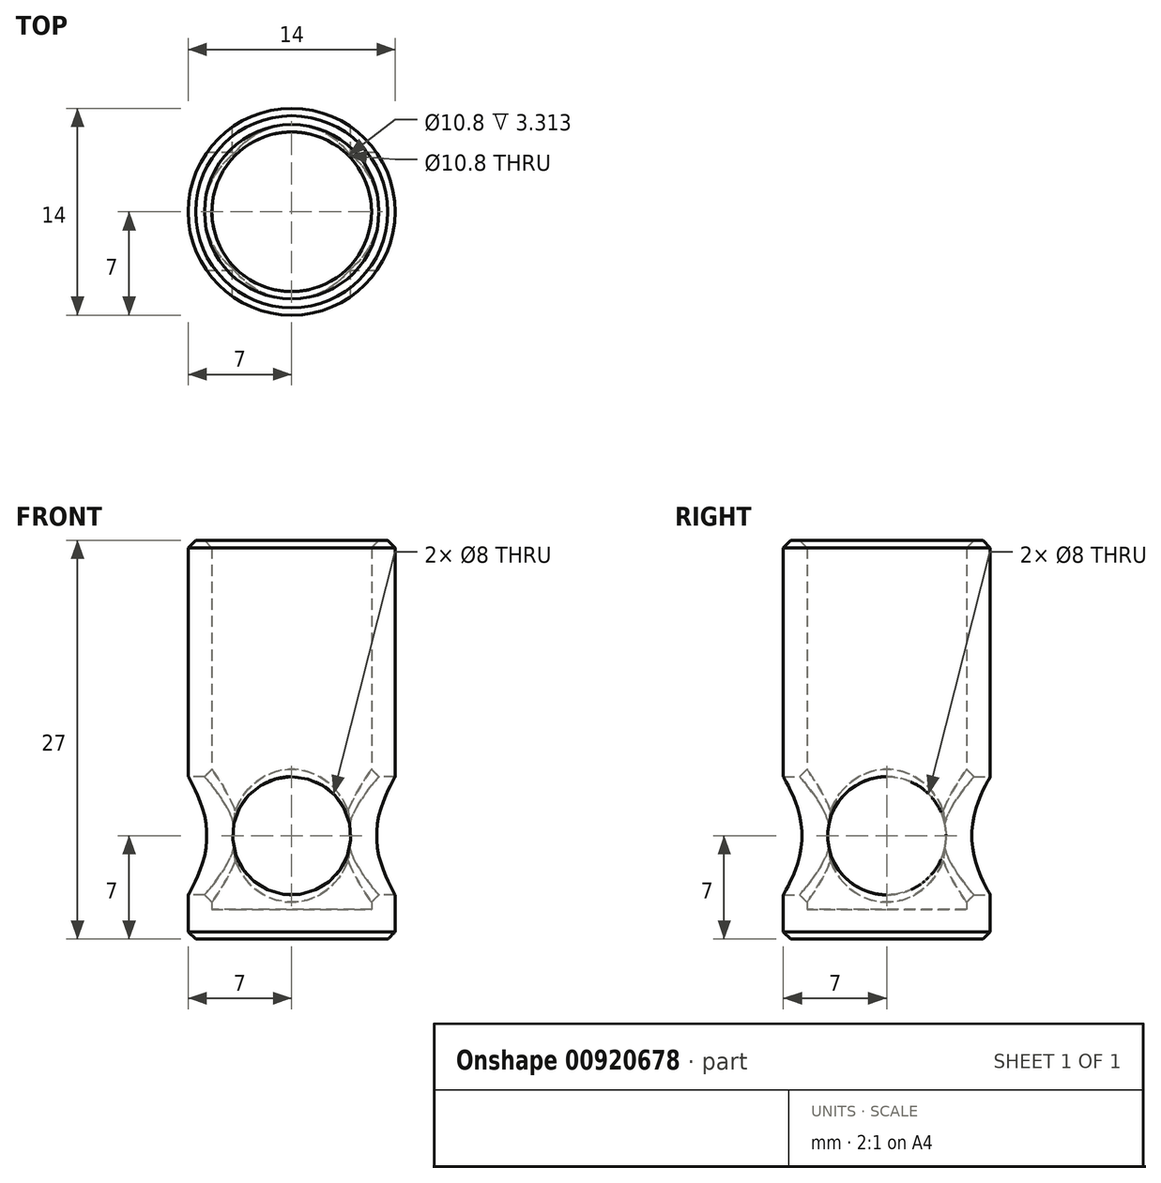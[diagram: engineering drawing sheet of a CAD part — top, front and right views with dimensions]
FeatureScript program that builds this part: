
annotation { "Feature Type Name" : "Feature", "Feature Type Description" : "" }
export const myFeature = defineFeature(function(context is Context, id is Id, definition is map)
    precondition{}
    {
        {
            var Q0;
            Q0=qCreatedBy(makeId("Top.planeOp"),FACE);
            var sketch = newSketch(context, id + "F0", { "sketchPlane" : qUnion([Q0])});
            skCircle(sketch, "E0", {"center": v(0, 0) * mm, "radius": 5.4 * mm});
            skCircle(sketch, "E1", {"center": v(0, 0) * mm, "radius": 7 * mm});
            skSolve(sketch);
        }
        {
            var Q0;
            Q0=makeQuery(id+"F0.imprint","IMPRINT",FACE,{"disambiguationData":[TD([[makeQuery(id+"F0.imprint","IMPRINT",EDGE,{"derivedFrom":sQuery(id+"F0.wireOp",EDGE,"E0")}),-1.0]])]});
            extrude(context, id + "F1", {"entities" : qUnion([Q0]), "depth" : 25 * mm, "offsetDistance" : 25 * mm});
        }
        {
            var Q0;
            Q0=makeQuery(id+"F1.opExtrude","CAP_FACE",FACE,{"disambiguationData":[OSD([sQuery(id+"F0.wireOp",EDGE,"E0"),sQuery(id+"F0.wireOp",EDGE,"E1")])],"isStart":true});
            var Q1;
            Q1=makeQuery(id+"F0.imprint","IMPRINT",FACE,{"disambiguationData":[TD([[makeQuery(id+"F0.imprint","IMPRINT",EDGE,{"derivedFrom":sQuery(id+"F0.wireOp",EDGE,"E0")}),1.0]])]});
            extrude(context, id + "F2", {"entities" : qUnion([Q0, Q1]), "operationType" : NewBodyOperationType.ADD, "depth" : 2 * mm, "offsetDistance" : 25 * mm});
        }
        {
            var Q0;
            Q0=qCreatedBy(makeId("Front.planeOp"),FACE);
            var sketch = newSketch(context, id + "F3", { "sketchPlane" : qUnion([Q0])});
            skPoint(sketch, "E2", {"position": v(0, 0) * mm});
            skPoint(sketch, "E3", {"position": v(0, 5) * mm});
            skCircle(sketch, "E4", {"center": v(0, 5) * mm, "radius": 4 * mm});
            skSolve(sketch);
        }
        {
            var Q0;
            Q0=makeQuery(id+"F3.imprint","IMPRINT",FACE,{"disambiguationData":[TD([[makeQuery(id+"F3.imprint","IMPRINT",EDGE,{"derivedFrom":sQuery(id+"F3.wireOp",EDGE,"E4")}),1.0]])]});
            extrude(context, id + "F4", {"entities" : qUnion([Q0]), "operationType" : NewBodyOperationType.REMOVE, "endBound" : BoundingType.SYMMETRIC, "depth" : 25 * mm, "offsetDistance" : 25 * mm});
        }
        {
            var Q0;
            Q0=qCreatedBy(makeId("Right.planeOp"),FACE);
            var sketch = newSketch(context, id + "F5", { "sketchPlane" : qUnion([Q0])});
            skPoint(sketch, "E5", {"position": v(0, -3.33) * mm});
            skPoint(sketch, "E6", {"position": v(0, 5) * mm});
            skCircle(sketch, "E7", {"center": v(0, 5) * mm, "radius": 4 * mm});
            skSolve(sketch);
        }
        {
            var Q0;
            Q0=makeQuery(id+"F5.imprint","IMPRINT",FACE,{"disambiguationData":[TD([[makeQuery(id+"F5.imprint","IMPRINT",EDGE,{"derivedFrom":sQuery(id+"F5.wireOp",EDGE,"E7")}),1.0]])]});
            extrude(context, id + "F6", {"entities" : qUnion([Q0]), "operationType" : NewBodyOperationType.REMOVE, "endBound" : BoundingType.SYMMETRIC, "depth" : 25 * mm, "offsetDistance" : 25 * mm});
        }
        {
            var Q0;
            Q0=makeQuery(id+"F1.opExtrude","CAP_EDGE",EDGE,{"disambiguationData":[OSD([sQuery(id+"F0.wireOp",EDGE,"E0")])],"isStart":false});
            var Q1;
            Q1=makeQuery(id+"F1.opExtrude","CAP_EDGE",EDGE,{"disambiguationData":[OSD([sQuery(id+"F0.wireOp",EDGE,"E1")])],"isStart":false});
            var Q2;
            Q2=makeQuery(id+"F6.boolean.opBoolean","SPLIT",EDGE,{"disambiguationData":[OD(1.0)],"derivedFrom":makeQuery(id+"F4.boolean.opBoolean","INTERSECT",EDGE,{"disambiguationData":[OD(0.0)],"derivedFrom":[makeQuery(id+"F1.opExtrude","SWEPT_FACE",FACE,{"disambiguationData":[OSD([sQuery(id+"F0.wireOp",EDGE,"E0")])]}),makeQuery(id+"F4.opExtrude","SWEPT_FACE",FACE,{"disambiguationData":[OSD([sQuery(id+"F3.wireOp",EDGE,"E4")])]})]})});
            var Q3;
            Q3=makeQuery(id+"F6.boolean.opBoolean","INTERSECT",EDGE,{"disambiguationData":[OD(3.0)],"derivedFrom":[makeQuery(id+"F1.opExtrude","SWEPT_FACE",FACE,{"disambiguationData":[OSD([sQuery(id+"F0.wireOp",EDGE,"E0")])]}),makeQuery(id+"F6.opExtrude","SWEPT_FACE",FACE,{"disambiguationData":[OSD([sQuery(id+"F5.wireOp",EDGE,"E7")])]})]});
            var Q4;
            Q4=makeQuery(id+"F6.boolean.opBoolean","SPLIT",EDGE,{"disambiguationData":[OD(1.0)],"derivedFrom":makeQuery(id+"F4.boolean.opBoolean","INTERSECT",EDGE,{"disambiguationData":[OD(1.0)],"derivedFrom":[makeQuery(id+"F1.opExtrude","SWEPT_FACE",FACE,{"disambiguationData":[OSD([sQuery(id+"F0.wireOp",EDGE,"E0")])]}),makeQuery(id+"F4.opExtrude","SWEPT_FACE",FACE,{"disambiguationData":[OSD([sQuery(id+"F3.wireOp",EDGE,"E4")])]})]})});
            var Q5;
            Q5=makeQuery(id+"F6.boolean.opBoolean","INTERSECT",EDGE,{"disambiguationData":[OD(2.0)],"derivedFrom":[makeQuery(id+"F1.opExtrude","SWEPT_FACE",FACE,{"disambiguationData":[OSD([sQuery(id+"F0.wireOp",EDGE,"E0")])]}),makeQuery(id+"F6.opExtrude","SWEPT_FACE",FACE,{"disambiguationData":[OSD([sQuery(id+"F5.wireOp",EDGE,"E7")])]})]});
            var Q6;
            Q6=makeQuery(id+"F1.opExtrude","CAP_EDGE",EDGE,{"disambiguationData":[OSD([sQuery(id+"F0.wireOp",EDGE,"E0")])],"isStart":true});
            var Q7;
            Q7=makeQuery(id+"F6.boolean.opBoolean","SPLIT",EDGE,{"disambiguationData":[OD(0.0)],"derivedFrom":makeQuery(id+"F4.boolean.opBoolean","INTERSECT",EDGE,{"disambiguationData":[OD(0.0)],"derivedFrom":[makeQuery(id+"F1.opExtrude","SWEPT_FACE",FACE,{"disambiguationData":[OSD([sQuery(id+"F0.wireOp",EDGE,"E0")])]}),makeQuery(id+"F4.opExtrude","SWEPT_FACE",FACE,{"disambiguationData":[OSD([sQuery(id+"F3.wireOp",EDGE,"E4")])]})]})});
            var Q8;
            Q8=makeQuery(id+"F6.boolean.opBoolean","INTERSECT",EDGE,{"disambiguationData":[OD(0.0)],"derivedFrom":[makeQuery(id+"F1.opExtrude","SWEPT_FACE",FACE,{"disambiguationData":[OSD([sQuery(id+"F0.wireOp",EDGE,"E0")])]}),makeQuery(id+"F6.opExtrude","SWEPT_FACE",FACE,{"disambiguationData":[OSD([sQuery(id+"F5.wireOp",EDGE,"E7")])]})]});
            var Q9;
            Q9=makeQuery(id+"F6.boolean.opBoolean","INTERSECT",EDGE,{"disambiguationData":[OD(1.0)],"derivedFrom":[makeQuery(id+"F1.opExtrude","SWEPT_FACE",FACE,{"disambiguationData":[OSD([sQuery(id+"F0.wireOp",EDGE,"E0")])]}),makeQuery(id+"F6.opExtrude","SWEPT_FACE",FACE,{"disambiguationData":[OSD([sQuery(id+"F5.wireOp",EDGE,"E7")])]})]});
            var Q10;
            Q10=makeQuery(id+"F6.boolean.opBoolean","SPLIT",EDGE,{"disambiguationData":[OD(0.0)],"derivedFrom":makeQuery(id+"F4.boolean.opBoolean","INTERSECT",EDGE,{"disambiguationData":[OD(1.0)],"derivedFrom":[makeQuery(id+"F1.opExtrude","SWEPT_FACE",FACE,{"disambiguationData":[OSD([sQuery(id+"F0.wireOp",EDGE,"E0")])]}),makeQuery(id+"F4.opExtrude","SWEPT_FACE",FACE,{"disambiguationData":[OSD([sQuery(id+"F3.wireOp",EDGE,"E4")])]})]})});
            var Q11;
            Q11=makeQuery(id+"F2.opExtrude","CAP_EDGE",EDGE,{"disambiguationData":[OSD([sQuery(id+"F0.wireOp",EDGE,"E1")])],"isStart":false});
            chamfer(context, id + "F7", {"entities" : qUnion([Q0, Q1, Q2, Q3, Q4, Q5, Q6, Q7, Q8, Q9, Q10, Q11]), "width" : 0.5 * mm, "tangentPropagation" : true});
        }
    });
